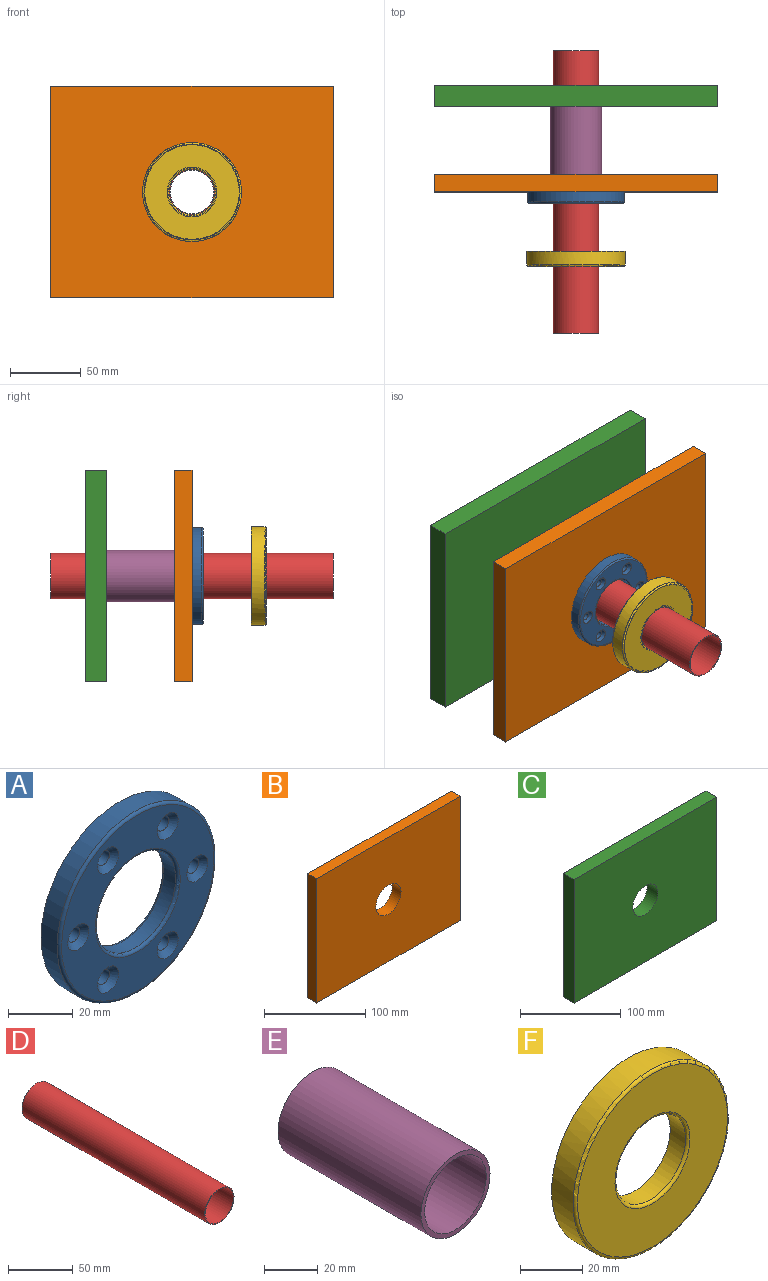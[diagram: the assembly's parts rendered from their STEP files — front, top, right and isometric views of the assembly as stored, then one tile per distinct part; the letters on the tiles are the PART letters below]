
ASSEMBLY  parts=6 mates=5
PART A: 21 faces, bbox 74.1x8x74.1 mm
  f0: cylinder r=2.62mm len=5.25mm, axis (0,1,0), area 86.6mm2, adj f11,f17
  f1: cylinder r=2.62mm len=5.25mm, axis (0,1,0), area 86.6mm2, adj f11,f16
  f2: cylinder r=2.62mm len=5.25mm, axis (0,1,0), area 86.6mm2, adj f11,f15
  f3: cylinder r=2.62mm len=5.25mm, axis (0,1,0), area 86.6mm2, adj f11,f20
  f4: cylinder r=2.62mm len=5.25mm, axis (0,1,0), area 86.6mm2, adj f11,f19
  f5: cylinder r=2.62mm len=5.25mm, axis (0,1,0), area 86.6mm2, adj f11,f18
  f6: cylinder r=17.5mm len=35mm, axis (0,1,0), area 577.3mm2, adj f12,f13
  f7: cylinder r=34.25mm len=68.5mm, axis (0,1,0), area 1506.4mm2, adj f9,f14
  f8: plane 66.5x66.5mm, normal (0,-1,0), area 1994.8mm2, adj f13,f14,f15,f16,f17,f18,f19,f20
  f9: plane 68.5x68.5mm, normal (0,1,0), area 367mm2, adj f7,f10
  f10: cylinder r=32.5mm len=65mm, axis (0,1,0), area 153.2mm2, adj f9,f11
  f11: plane 65x65mm, normal (0,1,0), area 2113.2mm2, adj f0,f1,f2,f3,f4,f5,f10,f12
  f12: torus R=18.5mm, axis (0,1,0), area 176.3mm2, adj f6,f11
  f13: torus R=18.5mm, axis (0,-1,0), area 176.3mm2, adj f6,f8
  f14: torus R=33.25mm, axis (0,-1,0), area 334.4mm2, adj f7,f8
  f15: cone r=2.62mm half-angle=45deg, axis (0,-1,0), area 64.4mm2, adj f2,f8
  f16: cone r=2.62mm half-angle=45deg, axis (0,-1,0), area 64.4mm2, adj f1,f8
  f17: cone r=2.62mm half-angle=45deg, axis (0,-1,0), area 64.4mm2, adj f0,f8
  f18: cone r=2.62mm half-angle=45deg, axis (0,-1,0), area 64.4mm2, adj f5,f8
  f19: cone r=2.62mm half-angle=45deg, axis (0,-1,0), area 64.4mm2, adj f4,f8
  f20: cone r=2.62mm half-angle=45deg, axis (0,-1,0), area 64.4mm2, adj f3,f8
PART B: 7 faces, bbox 200x12.5x150 mm
  f0: plane 200x12.5mm, normal (0,0,1), area 2500mm2, adj f1,f4,f5,f6
  f1: plane 150x12.5mm, normal (-1,0,0), area 1875mm2, adj f0,f2,f5,f6
  f2: plane 200x12.5mm, normal (0,0,-1), area 2500mm2, adj f1,f4,f5,f6
  f3: cylinder r=17.5mm len=35mm, axis (0,1,0), area 1374.4mm2, adj f5,f6
  f4: plane 150x12.5mm, normal (1,0,0), area 1875mm2, adj f0,f2,f5,f6
  f5: plane 200x150mm, normal (0,-1,0), area 29037.9mm2, adj f0,f1,f2,f3,f4
  f6: plane 200x150mm, normal (0,1,0), area 29037.9mm2, adj f0,f1,f2,f3,f4
PART C: 7 faces, bbox 200x15x150 mm
  f0: plane 200x15mm, normal (0,0,1), area 3000mm2, adj f1,f4,f5,f6
  f1: plane 150x15mm, normal (-1,0,0), area 2250mm2, adj f0,f2,f5,f6
  f2: plane 200x15mm, normal (0,0,-1), area 3000mm2, adj f1,f4,f5,f6
  f3: cylinder r=17.5mm len=35mm, axis (0,1,0), area 1649.3mm2, adj f5,f6
  f4: plane 150x15mm, normal (1,0,0), area 2250mm2, adj f0,f2,f5,f6
  f5: plane 200x150mm, normal (0,-1,0), area 29037.9mm2, adj f0,f1,f2,f3,f4
  f6: plane 200x150mm, normal (0,1,0), area 29037.9mm2, adj f0,f1,f2,f3,f4
PART D: 4 faces, bbox 32x200x32 mm
  f0: cylinder r=15.45mm len=200mm, axis (0,1,0), area 19415mm2, adj f2,f3
  f1: cylinder r=16mm len=200mm, axis (0,1,0), area 20106.2mm2, adj f2,f3
  f2: plane 32x32mm, normal (0,-1,0), area 54.3mm2, adj f0,f1
  f3: plane 32x32mm, normal (0,1,0), area 54.3mm2, adj f0,f1
PART E: 4 faces, bbox 36.5x75.5x36.5 mm
  f0: cylinder r=16.25mm len=75.5mm, axis (0,1,0), area 7708.7mm2, adj f2,f3
  f1: cylinder r=18.25mm len=75.5mm, axis (0,1,0), area 8657.4mm2, adj f2,f3
  f2: plane 36.5x36.5mm, normal (0,-1,0), area 216.8mm2, adj f0,f1
  f3: plane 36.5x36.5mm, normal (0,1,0), area 216.8mm2, adj f0,f1
PART F: 12 faces, bbox 75.8x10.8x75.8 mm
  f0: cylinder r=16.55mm len=33.1mm, axis (0,-1,0), area 670.7mm2, adj f7,f8
  f1: plane 66.9x66.9mm, normal (0,1,0), area 2547.5mm2, adj f8,f9
  f2: cylinder r=34.45mm len=68.9mm, axis (0,-1,0), area 1991.4mm2, adj f3,f9
  f3: plane 70x70mm, normal (0,1,0), area 120mm2, adj f2,f4
  f4: cylinder r=35mm len=70mm, axis (0,-1,0), area 2144.1mm2, adj f3,f10
  f5: plane 68x68mm, normal (0,-1,0), area 2723.8mm2, adj f10,f11
  f6: cylinder r=16mm len=32mm, axis (0,-1,0), area 703.7mm2, adj f7,f11
  f7: plane 33.1x33.1mm, normal (0,1,0), area 56.2mm2, adj f0,f6
  f8: torus R=17.55mm, axis (0,-1,0), area 166.9mm2, adj f0,f1
  f9: torus R=33.45mm, axis (0,-1,0), area 336.4mm2, adj f1,f2
  f10: torus R=34mm, axis (0,1,0), area 341.8mm2, adj f4,f5
  f11: torus R=17mm, axis (0,1,0), area 161.5mm2, adj f5,f6
PLACE A at identity
PLACE B at identity fixed
PLACE C rot(axis=(1,0,0),180deg) t=(0,48,0)mm
PLACE D t=(0,87.5,0)mm
PLACE E t=(0,63,0)mm
PLACE F t=(0,-64.64,0)mm
MATE fastened D.f1 <-> B.f3  axis (0,1,0) through (0,-12.5,0)mm
MATE slider F.f0 <-> D.f1  axis (0,-1,0) through (0,-60.69,0)mm
MATE fastened A.f10 <-> B.f3  axis (0,1,0) through (0,-12.5,0)mm
MATE fastened C.f3 <-> B.f3  axis (0,-1,0) through (0,48,0)mm
MATE fastened E.f0 <-> B.f3  axis (0,1,0) through (0,-12.5,0)mm
